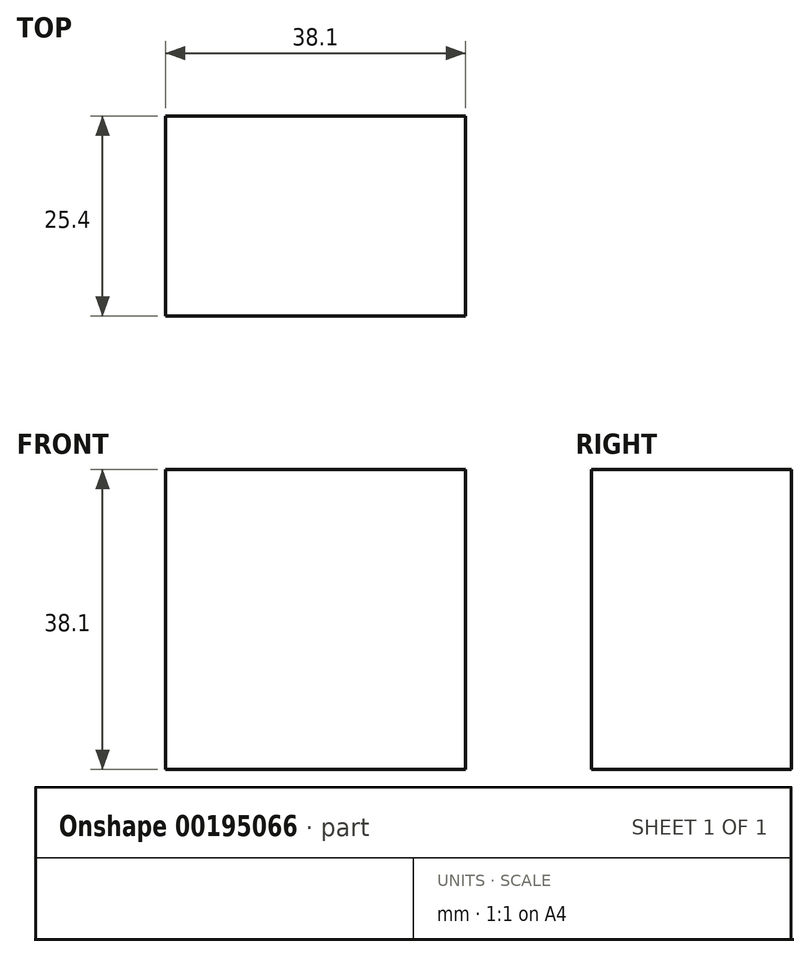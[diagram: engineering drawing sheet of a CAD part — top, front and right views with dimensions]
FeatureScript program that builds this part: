
annotation { "Feature Type Name" : "Feature", "Feature Type Description" : "" }
export const myFeature = defineFeature(function(context is Context, id is Id, definition is map)
    precondition{}
    {
        {
            var Q0;
            Q0=qCreatedBy(makeId("Front.planeOp"),FACE);
            var sketch = newSketch(context, id + "F0", { "sketchPlane" : qUnion([Q0])});
            skLineSegment(sketch, "E0.bottom", {"start": v(19.05, 19.05) * mm, "end": v(-19.05, 19.05) * mm});
            skLineSegment(sketch, "E0.top", {"start": v(19.05, -19.05) * mm, "end": v(-19.05, -19.05) * mm});
            skLineSegment(sketch, "E0.left", {"start": v(19.05, 19.05) * mm, "end": v(19.05, -19.05) * mm});
            skLineSegment(sketch, "E0.right", {"start": v(-19.05, 19.05) * mm, "end": v(-19.05, -19.05) * mm});
            skPoint(sketch, "E0.middle", {"position": v(0, 0) * mm});
            skSolve(sketch);
        }
        {
            var Q0;
            Q0=makeQuery(id+"F0.imprint","IMPRINT",FACE,{"disambiguationData":[TD([[makeQuery(id+"F0.imprint","IMPRINT",EDGE,{"derivedFrom":sQuery(id+"F0.wireOp",EDGE,"E0.bottom")}),1.0]])]});
            extrude(context, id + "F1", {"entities" : qUnion([Q0]), "oppositeDirection" : true, "depth" : 25.4 * mm});
        }
    });
